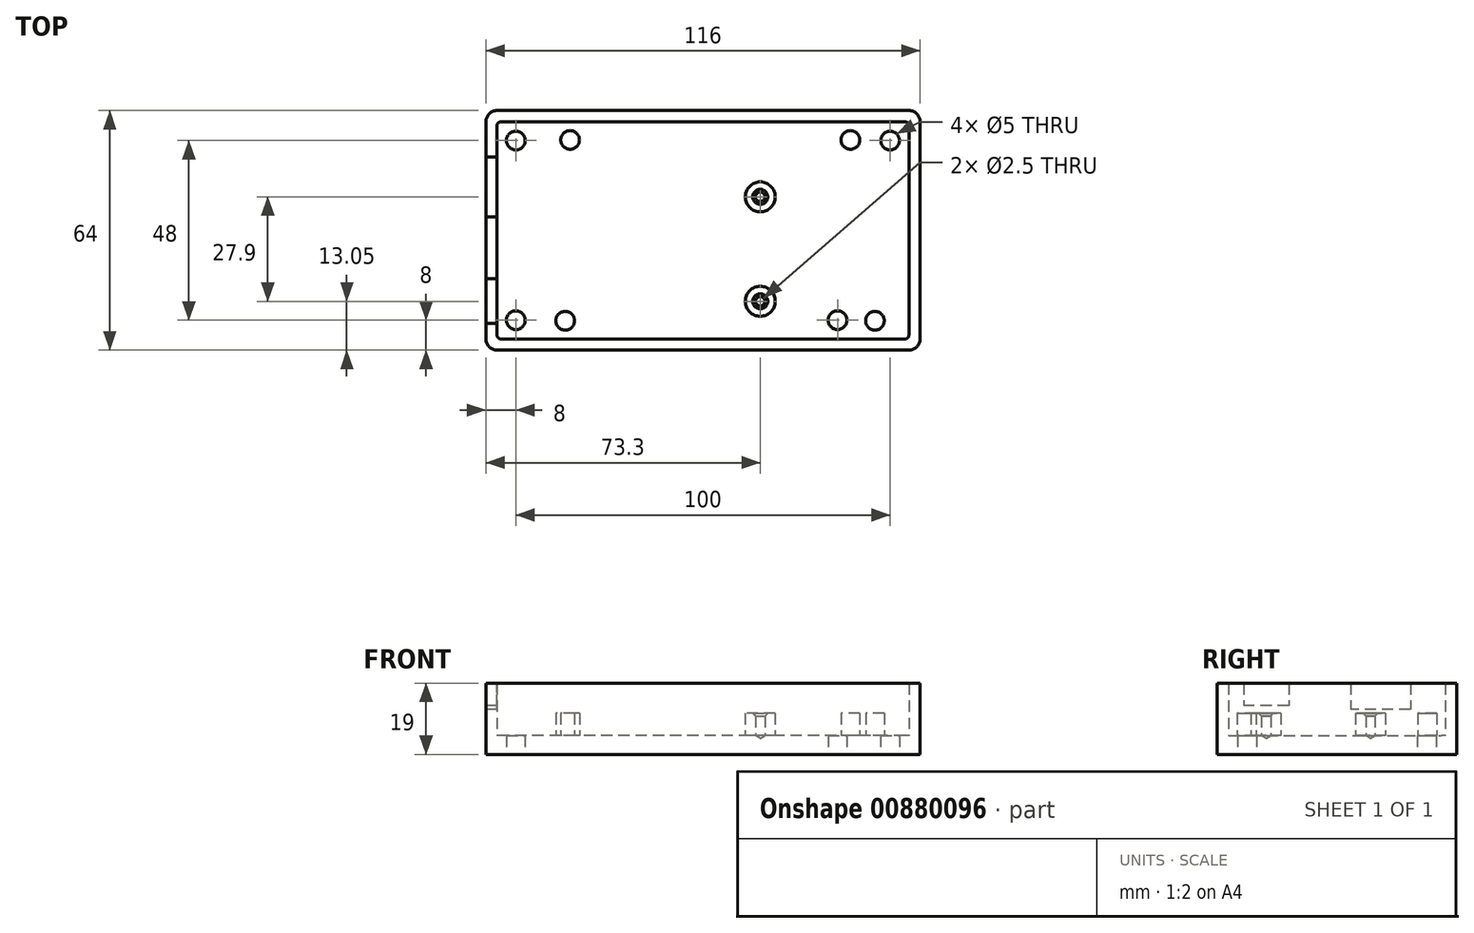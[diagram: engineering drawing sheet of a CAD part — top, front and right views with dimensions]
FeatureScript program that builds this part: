
annotation { "Feature Type Name" : "Feature", "Feature Type Description" : "" }
export const myFeature = defineFeature(function(context is Context, id is Id, definition is map)
    precondition{}
    {
        {
            var Q0;
            Q0=qCreatedBy(makeId("Top.planeOp"),FACE);
            var sketch = newSketch(context, id + "F0", { "sketchPlane" : qUnion([Q0])});
            skCircle(sketch, "E0", {"center": v(-36.8, -24.15) * mm, "radius": 1.59 * mm, "construction": true});
            skCircle(sketch, "E1", {"center": v(39.4, 24.15) * mm, "radius": 1.59 * mm, "construction": true});
            skCircle(sketch, "E2", {"center": v(15.3, 8.95) * mm, "radius": 1.59 * mm, "construction": true});
            skCircle(sketch, "E3", {"center": v(-35.5, 24.15) * mm, "radius": 1.59 * mm, "construction": true});
            skCircle(sketch, "E4", {"center": v(15.3, -18.95) * mm, "radius": 1.59 * mm, "construction": true});
            skCircle(sketch, "E5", {"center": v(45.95, -24.15) * mm, "radius": 1.59 * mm, "construction": true});
            skLineSegment(sketch, "E6", {"start": v(-50.8, 26.65) * mm, "end": v(45.7, 26.65) * mm, "construction": true});
            skLineSegment(sketch, "E7", {"start": v(45.7, 26.65) * mm, "end": v(48.23, 24.1) * mm, "construction": true});
            skLineSegment(sketch, "E8", {"start": v(48.23, 24.1) * mm, "end": v(48.23, 13.95) * mm, "construction": true});
            skLineSegment(sketch, "E9", {"start": v(48.26, 13.96) * mm, "end": v(50.8, 11.42) * mm, "construction": true});
            skLineSegment(sketch, "E10", {"start": v(50.8, 11.42) * mm, "end": v(50.8, -22.87) * mm, "construction": true});
            skLineSegment(sketch, "E11", {"start": v(48.23, -26.65) * mm, "end": v(-50.8, -26.65) * mm, "construction": true});
            skLineSegment(sketch, "E12", {"start": v(-52.6, -23.35) * mm, "end": v(-38.35, -23.35) * mm, "construction": true});
            skLineSegment(sketch, "E13", {"start": v(-38.35, -23.35) * mm, "end": v(-38.35, -14.35) * mm, "construction": true});
            skLineSegment(sketch, "E14", {"start": v(-38.35, -14.35) * mm, "end": v(-52.6, -14.35) * mm, "construction": true});
            skLineSegment(sketch, "E15", {"start": v(-52.6, -14.35) * mm, "end": v(-52.6, -23.35) * mm, "construction": true});
            skLineSegment(sketch, "E16", {"start": v(-57.8, 5.65) * mm, "end": v(-41.3, 5.65) * mm, "construction": true});
            skLineSegment(sketch, "E17", {"start": v(-41.3, 5.65) * mm, "end": v(-41.3, 17.65) * mm, "construction": true});
            skLineSegment(sketch, "E18", {"start": v(-41.3, 17.65) * mm, "end": v(-57.8, 17.65) * mm, "construction": true});
            skLineSegment(sketch, "E19", {"start": v(-57.8, 17.65) * mm, "end": v(-57.8, 5.65) * mm, "construction": true});
            skLineSegment(sketch, "E20", {"start": v(48.23, -26.65) * mm, "end": v(48.23, -25.38) * mm, "construction": true});
            skLineSegment(sketch, "E21", {"start": v(48.23, -25.38) * mm, "end": v(50.77, -22.84) * mm, "construction": true});
            skPoint(sketch, "E22", {"position": v(0, 0) * mm});
            skLineSegment(sketch, "E23", {"start": v(0, 0) * mm, "end": v(0, 0) * mm});
            skLineSegment(sketch, "E24", {"start": v(0, 26.65) * mm, "end": v(0, -26.65) * mm, "construction": true});
            skLineSegment(sketch, "E25", {"start": v(-50.8, 0) * mm, "end": v(50.8, 0) * mm, "construction": true});
            skLineSegment(sketch, "E26", {"start": v(15.3, 26.65) * mm, "end": v(15.3, -26.65) * mm, "construction": true});
            skLineSegment(sketch, "E27", {"start": v(-50.8, 24.15) * mm, "end": v(39.4, 24.15) * mm, "construction": true});
            skLineSegment(sketch, "E28", {"start": v(-50.8, -24.15) * mm, "end": v(45.95, -24.15) * mm, "construction": true});
            skLineSegment(sketch, "E29", {"start": v(-36.8, -24.15) * mm, "end": v(-36.8, 26.65) * mm, "construction": true});
            skLineSegment(sketch, "E30", {"start": v(-50.8, 26.65) * mm, "end": v(-50.8, -26.65) * mm, "construction": true});
            skPoint(sketch, "E31", {"position": v(-50.8, 17.65) * mm});
            skPoint(sketch, "E32", {"position": v(-50.8, 5.65) * mm});
            skPoint(sketch, "E33", {"position": v(-50.8, -14.35) * mm});
            skPoint(sketch, "E34", {"position": v(-50.8, -23.35) * mm});
            skSolve(sketch);
        }
        {
            var Q0;
            Q0=qCreatedBy(makeId("Top.planeOp"),FACE);
            var sketch = newSketch(context, id + "F1", { "sketchPlane" : qUnion([Q0])});
            skPoint(sketch, "E35", {"position": v(-10, 89.37) * mm});
            skPoint(sketch, "E36.0", {"position": v(-35.5, 24.15) * mm});
            skPoint(sketch, "E36.1", {"position": v(39.4, 24.15) * mm});
            skPoint(sketch, "E36.2", {"position": v(15.3, 8.95) * mm});
            skPoint(sketch, "E36.3", {"position": v(15.3, -18.95) * mm});
            skPoint(sketch, "E36.4", {"position": v(45.95, -24.15) * mm});
            skPoint(sketch, "E36.5", {"position": v(-36.8, -24.15) * mm});
            skLineSegment(sketch, "E37.bottom", {"start": v(55, 32) * mm, "end": v(-55, 32) * mm});
            skLineSegment(sketch, "E37.top", {"start": v(55, -32) * mm, "end": v(-55, -32) * mm});
            skLineSegment(sketch, "E37.left", {"start": v(58, 29) * mm, "end": v(58, -29) * mm});
            skLineSegment(sketch, "E37.right", {"start": v(-58, 29) * mm, "end": v(-58, -29) * mm});
            skPoint(sketch, "E37.middle", {"position": v(0, 0) * mm});
            skLineSegment(sketch, "E38.bottom", {"start": v(54, -29) * mm, "end": v(-54, -29) * mm});
            skLineSegment(sketch, "E38.top", {"start": v(54, 29) * mm, "end": v(-54, 29) * mm});
            skLineSegment(sketch, "E38.left", {"start": v(55, -28) * mm, "end": v(55, 28) * mm});
            skLineSegment(sketch, "E38.right", {"start": v(-55, -28) * mm, "end": v(-55, 28) * mm});
            skPoint(sketch, "E39.visualSharp", {"position": v(58, 32) * mm});
            skArc(sketch, "E39.filletArc", {"start": v(58, 29) * mm, "mid": v(57.12, 31.12) * mm, "end": v(55, 32) * mm});
            skPoint(sketch, "E40.visualSharp", {"position": v(58, -32) * mm});
            skArc(sketch, "E40.filletArc", {"start": v(55, -32) * mm, "mid": v(57.12, -31.12) * mm, "end": v(58, -29) * mm});
            skPoint(sketch, "E41.visualSharp", {"position": v(-58, -32) * mm});
            skArc(sketch, "E41.filletArc", {"start": v(-58, -29) * mm, "mid": v(-57.12, -31.12) * mm, "end": v(-55, -32) * mm});
            skPoint(sketch, "E42.visualSharp", {"position": v(-58, 32) * mm});
            skArc(sketch, "E42.filletArc", {"start": v(-55, 32) * mm, "mid": v(-57.12, 31.12) * mm, "end": v(-58, 29) * mm});
            skArc(sketch, "E43.filletArc", {"start": v(-54, 29) * mm, "mid": v(-54.7, 28.7) * mm, "end": v(-55, 28) * mm});
            skArc(sketch, "E44.filletArc", {"start": v(-55, -28) * mm, "mid": v(-54.7, -28.7) * mm, "end": v(-54, -29) * mm});
            skArc(sketch, "E45.filletArc", {"start": v(55, 28) * mm, "mid": v(54.7, 28.7) * mm, "end": v(54, 29) * mm});
            skArc(sketch, "E46.filletArc", {"start": v(54, -29) * mm, "mid": v(54.7, -28.7) * mm, "end": v(55, -28) * mm});
            skSolve(sketch);
        }
        {
            var Q0;
            Q0=makeQuery(id+"F1.imprint","IMPRINT",FACE,{"disambiguationData":[TD([[makeQuery(id+"F1.imprint","IMPRINT",EDGE,{"derivedFrom":sQuery(id+"F1.wireOp",EDGE,"sAtREINb-G6C3-cQC0-ztag-l7hX6wgJw8K5")}),-1.0]])]});
            var Q1;
            {var subQ0=sQuery(id+"F1.wireOp",EDGE,"E38.top");var subQ1=sQuery(id+"F1.wireOp",EDGE,"sAtREINb-G6C3-cQC0-ztag-l7hX6wgJw8K5");var subQ2=makeQuery(id+"F1.imprint","INTERSECT",VERTEX,{"disambiguationData":[OD(0.0)],"derivedFrom":[subQ1,subQ0]});Q1=makeQuery(id+"F1.imprint","IMPRINT",FACE,{"disambiguationData":[TD([[makeQuery(id+"F1.imprint","IMPRINT",EDGE,{"disambiguationData":[TD([[subQ2,1.0]])],"derivedFrom":subQ1}),1.0]])]});}
            var Q2;
            Q2=makeQuery(id+"F1.imprint","IMPRINT",FACE,{"disambiguationData":[TD([[makeQuery(id+"F1.imprint","IMPRINT",EDGE,{"derivedFrom":sQuery(id+"F1.wireOp",EDGE,"E37.bottom")}),1.0]])]});
            var Q3;
            Q3=makeQuery(id+"F1.imprint","IMPRINT",FACE,{"disambiguationData":[TD([[makeQuery(id+"F1.imprint","IMPRINT",EDGE,{"derivedFrom":sQuery(id+"F1.wireOp",EDGE,"kwzV1KH9-YTyi-yEjF-Eryo-3SAAlQY15cqW")}),1.0]])]});
            var Q4;
            {var subQ0=sQuery(id+"F1.wireOp",EDGE,"E38.top");var subQ1=sQuery(id+"F1.wireOp",EDGE,"uQAkhSxg-l0cz-5iHZ-dalg-Pfqns9K5Qn4p");var subQ2=makeQuery(id+"F1.imprint","INTERSECT",VERTEX,{"disambiguationData":[OD(0.0)],"derivedFrom":[subQ1,subQ0]});Q4=makeQuery(id+"F1.imprint","IMPRINT",FACE,{"disambiguationData":[TD([[makeQuery(id+"F1.imprint","IMPRINT",EDGE,{"disambiguationData":[TD([[subQ2,1.0]])],"derivedFrom":subQ1}),1.0]])]});}
            var Q5;
            {var subQ0=sQuery(id+"F1.wireOp",EDGE,"E38.bottom");var subQ1=sQuery(id+"F1.wireOp",EDGE,"6Ms3Rswy-JH4a-hiAd-mDHd-WPQgp7XCBPuc");var subQ2=makeQuery(id+"F1.imprint","INTERSECT",VERTEX,{"disambiguationData":[OD(0.0)],"derivedFrom":[subQ1,subQ0]});Q5=makeQuery(id+"F1.imprint","IMPRINT",FACE,{"disambiguationData":[TD([[makeQuery(id+"F1.imprint","IMPRINT",EDGE,{"disambiguationData":[TD([[subQ2,-1.0]])],"derivedFrom":subQ1}),1.0]])]});}
            var Q6;
            Q6=makeQuery(id+"F1.imprint","IMPRINT",FACE,{"disambiguationData":[TD([[makeQuery(id+"F1.imprint","IMPRINT",EDGE,{"derivedFrom":sQuery(id+"F1.wireOp",EDGE,"z08rlFCl-TPMt-w93p-UbxN-tgyrLAkJByhb")}),1.0]])]});
            var Q7;
            {var subQ0=sQuery(id+"F1.wireOp",EDGE,"E38.bottom");var subQ1=sQuery(id+"F1.wireOp",EDGE,"pGO305EG-kSJh-8pxp-xEoX-J9k6RAFc4AJp");var subQ2=makeQuery(id+"F1.imprint","INTERSECT",VERTEX,{"disambiguationData":[OD(0.0)],"derivedFrom":[subQ1,subQ0]});Q7=makeQuery(id+"F1.imprint","IMPRINT",FACE,{"disambiguationData":[TD([[makeQuery(id+"F1.imprint","IMPRINT",EDGE,{"disambiguationData":[TD([[subQ2,-1.0]])],"derivedFrom":subQ1}),1.0]])]});}
            var Q8;
            Q8=makeQuery(id+"F1.imprint","IMPRINT",FACE,{"disambiguationData":[TD([[makeQuery(id+"F1.imprint","IMPRINT",EDGE,{"derivedFrom":sQuery(id+"F1.wireOp",EDGE,"E38.bottom")}),-1.0]])]});
            extrude(context, id + "F2", {"entities" : qUnion([Q0, Q1, Q2, Q3, Q4, Q5, Q6, Q7, Q8]), "depth" : 5 * mm, "offsetDistance" : 25 * mm});
        }
        {
            var Q0;
            Q0=makeQuery(id+"F2.opExtrude","CAP_FACE",FACE,{"disambiguationData":[OSD([sQuery(id+"F1.wireOp",EDGE,"E37.bottom"),sQuery(id+"F1.wireOp",EDGE,"E37.top"),sQuery(id+"F1.wireOp",EDGE,"E37.left"),sQuery(id+"F1.wireOp",EDGE,"E37.right"),sQuery(id+"F1.wireOp",EDGE,"E39.filletArc"),sQuery(id+"F1.wireOp",EDGE,"E40.filletArc"),sQuery(id+"F1.wireOp",EDGE,"E41.filletArc"),sQuery(id+"F1.wireOp",EDGE,"E42.filletArc")])],"isStart":false});
            var sketch = newSketch(context, id + "F3", { "sketchPlane" : qUnion([Q0])});
            skPoint(sketch, "E47.0", {"position": v(-35.5, 24.15) * mm});
            skPoint(sketch, "E47.1", {"position": v(39.4, 24.15) * mm});
            skPoint(sketch, "E47.2", {"position": v(15.3, 8.95) * mm});
            skPoint(sketch, "E47.3", {"position": v(45.95, -24.15) * mm});
            skPoint(sketch, "E47.4", {"position": v(15.3, -18.95) * mm});
            skPoint(sketch, "E47.5", {"position": v(-36.8, -24.15) * mm});
            skPoint(sketch, "E48.0", {"position": v(-10, 89.37) * mm});
            skLineSegment(sketch, "E48.7", {"start": v(55, 32) * mm, "end": v(-55, 32) * mm});
            skLineSegment(sketch, "E48.8", {"start": v(55, -32) * mm, "end": v(-55, -32) * mm});
            skLineSegment(sketch, "E48.9", {"start": v(58, 29) * mm, "end": v(58, -29) * mm});
            skLineSegment(sketch, "E48.10", {"start": v(-58, 29) * mm, "end": v(-58, -29) * mm});
            skPoint(sketch, "E48.11", {"position": v(0, 0) * mm});
            skLineSegment(sketch, "E48.12", {"start": v(54, -29) * mm, "end": v(-54, -29) * mm});
            skLineSegment(sketch, "E48.13", {"start": v(54, 29) * mm, "end": v(-54, 29) * mm});
            skLineSegment(sketch, "E48.14", {"start": v(55, -28) * mm, "end": v(55, 28) * mm});
            skLineSegment(sketch, "E48.15", {"start": v(-55, -28) * mm, "end": v(-55, 28) * mm});
            skPoint(sketch, "E48.16", {"position": v(0, 0) * mm});
            skPoint(sketch, "E48.17", {"position": v(58, 32) * mm});
            skArc(sketch, "E48.18", {"start": v(58, 29) * mm, "mid": v(57.12, 31.12) * mm, "end": v(55, 32) * mm});
            skPoint(sketch, "E48.19", {"position": v(58, -32) * mm});
            skArc(sketch, "E48.20", {"start": v(55, -32) * mm, "mid": v(57.12, -31.12) * mm, "end": v(58, -29) * mm});
            skPoint(sketch, "E48.21", {"position": v(-58, -32) * mm});
            skArc(sketch, "E48.22", {"start": v(-58, -29) * mm, "mid": v(-57.12, -31.12) * mm, "end": v(-55, -32) * mm});
            skPoint(sketch, "E48.23", {"position": v(-58, 32) * mm});
            skArc(sketch, "E48.24", {"start": v(-55, 32) * mm, "mid": v(-57.12, 31.12) * mm, "end": v(-58, 29) * mm});
            skPoint(sketch, "E48.25", {"position": v(-55, 29) * mm});
            skArc(sketch, "E48.26", {"start": v(-54, 29) * mm, "mid": v(-54.7, 28.7) * mm, "end": v(-55, 28) * mm});
            skPoint(sketch, "E48.27", {"position": v(-55, -29) * mm});
            skArc(sketch, "E48.28", {"start": v(-55, -28) * mm, "mid": v(-54.7, -28.7) * mm, "end": v(-54, -29) * mm});
            skPoint(sketch, "E48.29", {"position": v(55, 29) * mm});
            skArc(sketch, "E48.30", {"start": v(55, 28) * mm, "mid": v(54.7, 28.7) * mm, "end": v(54, 29) * mm});
            skPoint(sketch, "E48.31", {"position": v(55, -29) * mm});
            skArc(sketch, "E48.32", {"start": v(54, -29) * mm, "mid": v(54.7, -28.7) * mm, "end": v(55, -28) * mm});
            skCircle(sketch, "E49", {"center": v(-35.5, 24.15) * mm, "radius": 2.5 * mm});
            skCircle(sketch, "E50", {"center": v(39.4, 24.15) * mm, "radius": 2.5 * mm});
            skCircle(sketch, "E51", {"center": v(15.3, 8.95) * mm, "radius": 4 * mm});
            skCircle(sketch, "E52", {"center": v(45.95, -24.15) * mm, "radius": 2.5 * mm});
            skCircle(sketch, "E53", {"center": v(-36.8, -24.15) * mm, "radius": 2.5 * mm});
            skCircle(sketch, "E54", {"center": v(15.3, -18.95) * mm, "radius": 4 * mm});
            skPoint(sketch, "E55", {"position": v(-50, 24) * mm});
            skPoint(sketch, "E56.MirrorP", {"position": v(50, 24) * mm});
            skPoint(sketch, "E57.MirrorP", {"position": v(-50, -24) * mm});
            skPoint(sketch, "E58.MirrorP", {"position": v(35.95, -24) * mm});
            skSolve(sketch);
        }
        {
            var Q0;
            Q0 = qSketchRegion(id + "F3", true);
            extrude(context, id + "F4", {"entities" : qUnion([Q0]), "operationType" : NewBodyOperationType.ADD, "depth" : 14 * mm, "offsetDistance" : 25 * mm});
        }
        {
            var Q0;
            Q0 = qSketchRegion(id + "F3", true);
            var Q1;
            Q1=makeQuery(id+"F3.imprint","IMPRINT",FACE,{"disambiguationData":[TD([[makeQuery(id+"F3.imprint","IMPRINT",EDGE,{"derivedFrom":sQuery(id+"F3.wireOp",EDGE,"E49")}),1.0]])]});
            var Q2;
            Q2=makeQuery(id+"F3.imprint","IMPRINT",FACE,{"disambiguationData":[TD([[makeQuery(id+"F3.imprint","IMPRINT",EDGE,{"derivedFrom":sQuery(id+"F3.wireOp",EDGE,"E53")}),1.0]])]});
            var Q3;
            Q3=makeQuery(id+"F3.imprint","IMPRINT",FACE,{"disambiguationData":[TD([[makeQuery(id+"F3.imprint","IMPRINT",EDGE,{"derivedFrom":sQuery(id+"F3.wireOp",EDGE,"E51")}),1.0]])]});
            var Q4;
            Q4=makeQuery(id+"F3.imprint","IMPRINT",FACE,{"disambiguationData":[TD([[makeQuery(id+"F3.imprint","IMPRINT",EDGE,{"derivedFrom":sQuery(id+"F3.wireOp",EDGE,"E54")}),1.0]])]});
            var Q5;
            Q5=makeQuery(id+"F3.imprint","IMPRINT",FACE,{"disambiguationData":[TD([[makeQuery(id+"F3.imprint","IMPRINT",EDGE,{"derivedFrom":sQuery(id+"F3.wireOp",EDGE,"E52")}),1.0]])]});
            var Q6;
            Q6=makeQuery(id+"F3.imprint","IMPRINT",FACE,{"disambiguationData":[TD([[makeQuery(id+"F3.imprint","IMPRINT",EDGE,{"derivedFrom":sQuery(id+"F3.wireOp",EDGE,"E50")}),1.0]])]});
            extrude(context, id + "F5", {"entities" : qUnion([Q0, Q1, Q2, Q3, Q4, Q5, Q6]), "operationType" : NewBodyOperationType.ADD, "depth" : 6 * mm, "offsetDistance" : 25 * mm});
        }
        {
            var Q0;
            Q0=makeQuery(id+"F5.opExtrude","CAP_FACE",FACE,{"disambiguationData":[OSD([sQuery(id+"F3.wireOp",EDGE,"E49")])],"isStart":false});
            var sketch = newSketch(context, id + "F6", { "sketchPlane" : qUnion([Q0])});
            skPoint(sketch, "E59.0", {"position": v(-35.5, 24.15) * mm});
            skPoint(sketch, "E59.1", {"position": v(-36.8, -24.15) * mm});
            skPoint(sketch, "E59.2", {"position": v(15.3, -18.95) * mm});
            skPoint(sketch, "E59.3", {"position": v(15.3, 8.95) * mm});
            skPoint(sketch, "E59.4", {"position": v(39.4, 24.15) * mm});
            skPoint(sketch, "E59.5", {"position": v(45.95, -24.15) * mm});
            skSolve(sketch);
        }
        {
            var Q0;
            Q0=sQuery(id+"F6.wireOp",VERTEX,"E59.3");
            var Q1;
            Q1=sQuery(id+"F6.wireOp",VERTEX,"E59.2");
            var Q2;
            Q2=makeQuery(id+"F2.opExtrude","SWEPT_BODY",BODY,{"disambiguationData":[OSD([sQuery(id+"F1.wireOp",EDGE,"E37.bottom"),sQuery(id+"F1.wireOp",EDGE,"E37.top"),sQuery(id+"F1.wireOp",EDGE,"E37.left"),sQuery(id+"F1.wireOp",EDGE,"E37.right"),sQuery(id+"F1.wireOp",EDGE,"E39.filletArc"),sQuery(id+"F1.wireOp",EDGE,"E40.filletArc"),sQuery(id+"F1.wireOp",EDGE,"E41.filletArc"),sQuery(id+"F1.wireOp",EDGE,"E42.filletArc")])]});
            hole(context, id + "F7", {"style" : HoleStyle.C_SINK, "endStyle" : HoleEndStyle.BLIND, "holeDiameter" : 2.5 * mm, "cSinkDiameter" : 4 * mm, "cSinkAngle" : 90 * degree, "majorDiameter" : 5 * mm, "holeDepth" : 6 * mm, "isTappedThrough" : true, "tappedDepth" : 12 * mm, "tapClearance" : 3, "locations" : qUnion([Q0, Q1]), "scope" : qUnion([Q2])});
        }
        {
            var Q0;
            Q0=sQuery(id+"F3.wireOp",VERTEX,"E55");
            var Q1;
            Q1=sQuery(id+"F3.wireOp",VERTEX,"E56.MirrorP");
            var Q2;
            Q2=sQuery(id+"F3.wireOp",VERTEX,"E58.MirrorP");
            var Q3;
            Q3=sQuery(id+"F3.wireOp",VERTEX,"E57.MirrorP");
            var Q4;
            Q4=makeQuery(id+"F2.opExtrude","SWEPT_BODY",BODY,{"disambiguationData":[OSD([sQuery(id+"F1.wireOp",EDGE,"E37.bottom"),sQuery(id+"F1.wireOp",EDGE,"E37.top"),sQuery(id+"F1.wireOp",EDGE,"E37.left"),sQuery(id+"F1.wireOp",EDGE,"E37.right"),sQuery(id+"F1.wireOp",EDGE,"E39.filletArc"),sQuery(id+"F1.wireOp",EDGE,"E40.filletArc"),sQuery(id+"F1.wireOp",EDGE,"E41.filletArc"),sQuery(id+"F1.wireOp",EDGE,"E42.filletArc")])]});
            hole(context, id + "F8", {"style" : HoleStyle.SIMPLE, "endStyle" : HoleEndStyle.THROUGH, "holeDiameter" : 5 * mm, "majorDiameter" : 5 * mm, "isTappedThrough" : true, "tappedDepth" : 12 * mm, "tapClearance" : 3, "locations" : qUnion([Q0, Q1, Q2, Q3]), "scope" : qUnion([Q4])});
        }
        {
            var Q0;
            Q0=makeQuery(id+"F4.boolean.opBoolean","MERGE",FACE,{"derivedFrom":[makeQuery(id+"F2.opExtrude","SWEPT_FACE",FACE,{"disambiguationData":[OSD([sQuery(id+"F1.wireOp",EDGE,"E37.right")])]}),makeQuery(id+"F4.opExtrude","SWEPT_FACE",FACE,{"disambiguationData":[OSD([sQuery(id+"F3.wireOp",EDGE,"E48.10")])]})]});
            var sketch = newSketch(context, id + "F9", { "sketchPlane" : qUnion([Q0])});
            skPoint(sketch, "E60.0", {"position": v(-17.65, 0) * mm});
            skPoint(sketch, "E60.1", {"position": v(-5.65, 0) * mm});
            skPoint(sketch, "E60.2", {"position": v(14.35, 0) * mm});
            skPoint(sketch, "E60.3", {"position": v(23.35, 0) * mm});
            skLineSegment(sketch, "E61", {"start": v(-17.65, 0) * mm, "end": v(-17.65, 19) * mm, "construction": true});
            skLineSegment(sketch, "E62", {"start": v(-5.65, 0) * mm, "end": v(-5.65, 19) * mm, "construction": true});
            skLineSegment(sketch, "E63", {"start": v(14.35, 0) * mm, "end": v(14.35, 19) * mm, "construction": true});
            skLineSegment(sketch, "E64", {"start": v(23.35, 0) * mm, "end": v(23.35, 19) * mm, "construction": true});
            skLineSegment(sketch, "E65", {"start": v(-17.65, 19) * mm, "end": v(-5.65, 19) * mm, "construction": true});
            skLineSegment(sketch, "E66", {"start": v(14.35, 19) * mm, "end": v(23.35, 19) * mm, "construction": true});
            skPoint(sketch, "E67", {"position": v(-11.65, 19) * mm});
            skPoint(sketch, "E68", {"position": v(18.85, 19) * mm});
            skLineSegment(sketch, "E69.bottom", {"start": v(-19.65, 19) * mm, "end": v(-3.65, 19) * mm});
            skLineSegment(sketch, "E69.top", {"start": v(-19.65, 12) * mm, "end": v(-3.65, 12) * mm});
            skLineSegment(sketch, "E69.left", {"start": v(-19.65, 19) * mm, "end": v(-19.65, 12) * mm});
            skLineSegment(sketch, "E69.right", {"start": v(-3.65, 19) * mm, "end": v(-3.65, 12) * mm});
            skLineSegment(sketch, "E70.bottom", {"start": v(12.85, 19) * mm, "end": v(24.85, 19) * mm});
            skLineSegment(sketch, "E70.top", {"start": v(12.85, 13) * mm, "end": v(24.85, 13) * mm});
            skLineSegment(sketch, "E70.left", {"start": v(12.85, 19) * mm, "end": v(12.85, 13) * mm});
            skLineSegment(sketch, "E70.right", {"start": v(24.85, 19) * mm, "end": v(24.85, 13) * mm});
            skSolve(sketch);
        }
        {
            var Q0;
            Q0=makeQuery(id+"F9.imprint","IMPRINT",FACE,{"disambiguationData":[TD([[makeQuery(id+"F9.imprint","IMPRINT",EDGE,{"derivedFrom":sQuery(id+"F9.wireOp",EDGE,"E69.bottom")}),-1.0]])]});
            var Q1;
            Q1=makeQuery(id+"F9.imprint","IMPRINT",FACE,{"disambiguationData":[TD([[makeQuery(id+"F9.imprint","IMPRINT",EDGE,{"derivedFrom":sQuery(id+"F9.wireOp",EDGE,"E70.bottom")}),-1.0]])]});
            extrude(context, id + "F10", {"entities" : qUnion([Q0, Q1]), "operationType" : NewBodyOperationType.REMOVE, "endBound" : BoundingType.UP_TO_NEXT, "oppositeDirection" : true, "depth" : 25 * mm, "offsetDistance" : 25 * mm});
        }
    });
